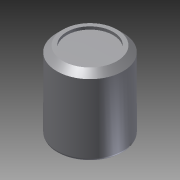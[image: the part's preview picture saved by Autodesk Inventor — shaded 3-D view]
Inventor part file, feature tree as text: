
AUTODESK INVENTOR PART (.ipt)
format: ipt  version: 2014 (Build 180170000, 170)  size: 179,200 bytes
history: native  units: in
note: dims shown in document units (in); Inventor stores cm internally (conversion verified against a paired STEP export)
features: other x42, sketch x4, revolve x3, extrude x1
ambient origin geometry x8: Origin, YZ Plane, XZ Plane, XY Plane, X Axis, Y Axis, Z Axis, Center Point
bodies: Solid1 (feature_tree)
feature tree (50):
  revolve  "Revolution1"  Angle=360.0deg
  revolve  "Revolution2"  Angle=360.0deg
  sketch  "Sketch_7"
  extrude  "Extrusion1"  [1 undecoded]
  revolve  "Revolution3"  [1 undecoded]
  other  "to_at504_knurled_face_nut_XY"
  other  "to_at504_knurled_face_nut_YZ"
  other  "to_at504_knurled_face_nut_ZX"
  other  "to_at504_knurled_face_nut_X"
  other  "to_at504_knurled_face_nut_Y"
  other  "to_at504_knurled_face_nut_Z"
  other  "to_at504_knurled_face_nut_Center"
  other  "to_at508_lockwasher_XY"
  other  "to_at508_lockwasher_YZ"
  other  "to_at508_lockwasher_ZX"
  other  "to_at508_lockwasher_X"
  other  "to_at508_lockwasher_Y"
  other  "to_at508_lockwasher_Z"
  other  "to_at508_lockwasher_Center"
  other  "to_dummy_XY"
  other  "to_dummy_YZ"
  other  "to_dummy_ZX"
  other  "to_dummy_X"
  other  "to_dummy_Y"
  other  "to_dummy_Z"
  other  "to_dummy_Center"
  other  "to_hex_nut_XY"
  other  "to_hex_nut_YZ"
  other  "to_hex_nut_ZX"
  other  "to_hex_nut_X"
  other  "to_hex_nut_Y"
  other  "to_hex_nut_Z"
  other  "to_hex_nut_Center"
  other  "to_plunger_XY"
  other  "to_plunger_YZ"
  other  "to_plunger_ZX"
  other  "to_plunger_X"
  other  "to_plunger_Y"
  other  "to_plunger_Z"
  other  "to_plunger_Center"
  other  "to_trmnl_hold_XY"
  other  "to_trmnl_hold_YZ"
  other  "to_trmnl_hold_ZX"
  other  "to_trmnl_hold_X"
  other  "to_trmnl_hold_Y"
  other  "to_trmnl_hold_Z"
  other  "to_trmnl_hold_Center"
  sketch  "Sketch_2"  dims[d0=360.0deg d1=360.0deg]
  sketch  "Sketch_3"  dims[d2=0.03in d3=0.0in d4=360.0deg]
  sketch  "Sketch_9"
note: 2 required parameter values undecoded (feature->parameter linkage not recoverable at this tier; creation-order binding heuristic only, values carry confidence <= 0.55)
